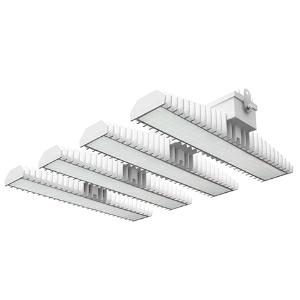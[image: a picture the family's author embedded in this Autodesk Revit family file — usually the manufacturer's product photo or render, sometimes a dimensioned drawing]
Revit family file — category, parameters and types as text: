
# Revit family: 3f_filippi_-_3f_lem_ampio_3f_filippi_-_58902_a0812_-_3f_lem_4_led_200_dali_cr_ampio___vs_4026
name_source: partatom
category: Lighting Fixtures
units: mm (PartAtom-declared; Revit-internal decimal feet)

## family parameters
Cut with Voids When Loaded = No
Host = Face
Light Source = No
Part Type = Normal
Room Calculation Point = No
Round Connector Dimension = Use Diameter
Shared = No

## types (1)
- 3F Filippi - 3F LEM Ampio (1 x LED, 26607 lm, 218 W, 4000 K)
    Apparent Load = 218 VA
    Approval mark = CE
    CIE Flux Codes = 67 90 97 100 100
    Color Rendering = 80
    Color Temperature = 4000 K
    Control Gear = Electronic transformer
    Default Elevation = 1800 mm
    Description = Industrial luminaire with high light output and high luminous efficiency designed with the most innovative technologies for environments with temperature up to 55°C.

ILLUMINOTECHNICAL
Luminous efficiency 100% (DLOR 98%, ULOR 2%).
Initial luminous flux of the luminaire 26607 lm.
Direct symmetric wide distribution: the illuminated area has a rectangular shape.
Installation Interdistance Transv.D = 1.24 x hu - Long.D = 1.20 x hu.
Tabular UGR (CIE 117 - 4H-8H; S=0.25H; 70/50/20): RUG 22.8 - 22.9.
Beam angle: 82° - 83°.
Luminous efficacy 122 lm/W.
Lifetime (L93/B10): 30000 h. (tq+25°C)
Lifetime (L90/B10): 50000 h. (tq+25°C)
Lifetime (L85/B10): 80000 h. (tq+25°C)
Lifetime (L80/B10): 100000 h. (tq+25°C)
Lifetime (L85/B10): 50000 h. (tq+55°C)
Sudden decreased luminous flux after 50000 hours: 0% (C0).
Photobiological safety in compliance with IEC/TR 62778: RG0 risk exempt, (IEC 62471).
In compliance with IEC/EN 62722-2-1 - IEC/EN 62717 standards.

SOURCE
4 Mid-Power linear LED modules 50W/840.
Energy efficiency class (UE 2019/2020 - UE 2019/2015): C.
CIE 13.3 Colour rendering index: CRI >80 (R9 <50%).
IES TM-30 Fidelity Index: Rf = 84 Rg = 95.
CCT nominal colour temperature 4000 K.
Colour initial tolerance (MacAdam): SDCM 3.

MECHANICAL
Passive modular heatsinks in die-casted aluminium, painted in white colour.
To optimize the thermal management of the LED module, the heatsinks are oversized and provided with self-cleaning of cooling fins.
Wiring body in aluminium and galvanised steel anchored solidly to the sinks and thermally separated.
3F Lens lenses with high luminous efficiency, transparent methacrylate (PMMA), fixed to the LED modules.
Fixing brackets in stainless steel.
Luminaire with limited surface temperature. - D - (EN 60598-2-24)
Dimensions: 757x542 mm, height 133 mm. Weight 19.385 kg.
IP65 protection degree.
Mechanical strength to impacts IK06 (1 joule).
Glow-wire test resistance 650°C.

ELECTRICAL
Halogen Free DALI-2 DATI (Parts 251, 252, 253), PUSH-DIM, electronic wiring 230V-50/60Hz, power factor 0.97 at full load, THD <25%, constant output current, class I, 2 driver, 2 DALI addresses.
Power of the luminaire 218 W.
ENEC - CE.
Flicker: <4%.
Luminaire compliant with EN 60598-2-22 for power supply from a centralised emergency system CPSS (Central Power Supply System), not incorporated in the luminaire - high risk areas excluded. The default power and flux are 100% in AC and 15% in DC.
Ambient temperature from -30°C to +55°C.
Temperature class T6 max 85°C.
Quick connection via M25 5P connector with 9-13 mm tightening range.
Power unit positioned on a separate compartment by the LED module to ensure optimum temperatures of cabling components, to be inspectable and maintainable.
Relative humidity UR: <85%.

INSTALLATION
Ceiling / Suspended / Wall.
All accessories dedicated to this product are available on the Catalog and on our website www.3F-Filippi.com.

ACCESSORIES
A0812 - Anti-glare microprismatic VS moulded glass, tempered, not flammable, with sealing gasket.
One required for each light module. The pack contains 10 pieces.

APPLICATIONS
In commercial environments, exhibition and industrial areas, stores, open areas.
Applications with high ambient temperature up to 55°C.
Environments in which it is necessary a total protection against falling fragments (eg environments with foodstuffs or machines with moving parts or with extreme temperature changes), use luminaires with polycarbonate lenses.

LIGHT MANAGEMENT
Recommended minimum setting: 10%.
The luminaire, equipped with (DALI-2 DATI) driver, can be controlled manually with 3F Easy Dim technology or automatically/manually with wired or wireless DALI/D2D control systems.
The D2D driver guarantees interoperability with other devices with the same certification by making the following information available:
Device Data (Part 251), Energy Report (Part 252), Diagnosis & Maintenance (Part 253).
In electrical systems without a regulation system (manual or automatic) and DALI bus, a suitable jumper must be made on the DA-DA terminals of the appliance.

WARNING
Fixture not suitable for cold stores with an ambient temperature <0°C and/or relative humidity >85%.
Luminaire designed for disposal/recycling at end-of-life.
Replaceable (LED only) light source by a professional. Replaceable control gear by a professional.
    Height = 133 mm  [stored 0.436352 ft]
    Lamp = 1 x LED
    Lamp Light Flux = 26607 lm
    Lamp Power = 218 W
    Lamp count = 1
    Length = 757 mm
    Lifetime = 50000 h
    Luminous efficacy = 122 lm/W
    Manufacturer = 3F Filippi
    ModVariant = No
    Model = 3F Filippi - 58902+A0812 - 3F LEM 4 LED 200 DALI CR AMPIO + VS
    Mounting Place = Ceiling
    Mounting Type = Pendant
    Number of Poles = 1
    OnlyDefault = Yes
    Power Factor = 1
    Product Name = 3F Filippi - 3F LEM Ampio
    Product group = pendant luminaire
    ProductGroupID = 9
    Protection Class = Protection class I
    Protection Degree = IP 65
    RLX_Detail_Level = 1
    RLX_Emergency_Light_Flux = 0 lm
    RLX_Emergency_Type = 0
    RLX_Emergency_Type_DB = No
    RlxData = <blob elided: 122297 chars, md5=2d24c95a>
    Socket = socket
    Standby Power = 0 W
    System Light Flux = 26607 lm
    System Power = 218 W
    Type Comments = Product without accessories
    Type Image = 3f_filippi_-_lem_4__a0812.jpg
    URL = http://relux.com
    VarID = ---
    Voltage = 0 V
    Weight = 0.00 kg
    Width = 542 mm

note: [stored X ft] marks values corroborated as IEEE doubles in the binary element streams (Revit-internal decimal feet)

## geometry (parser evidence)
native form markers: Blend x4, Sweep x13
no freeform markers — native parametric forms only
